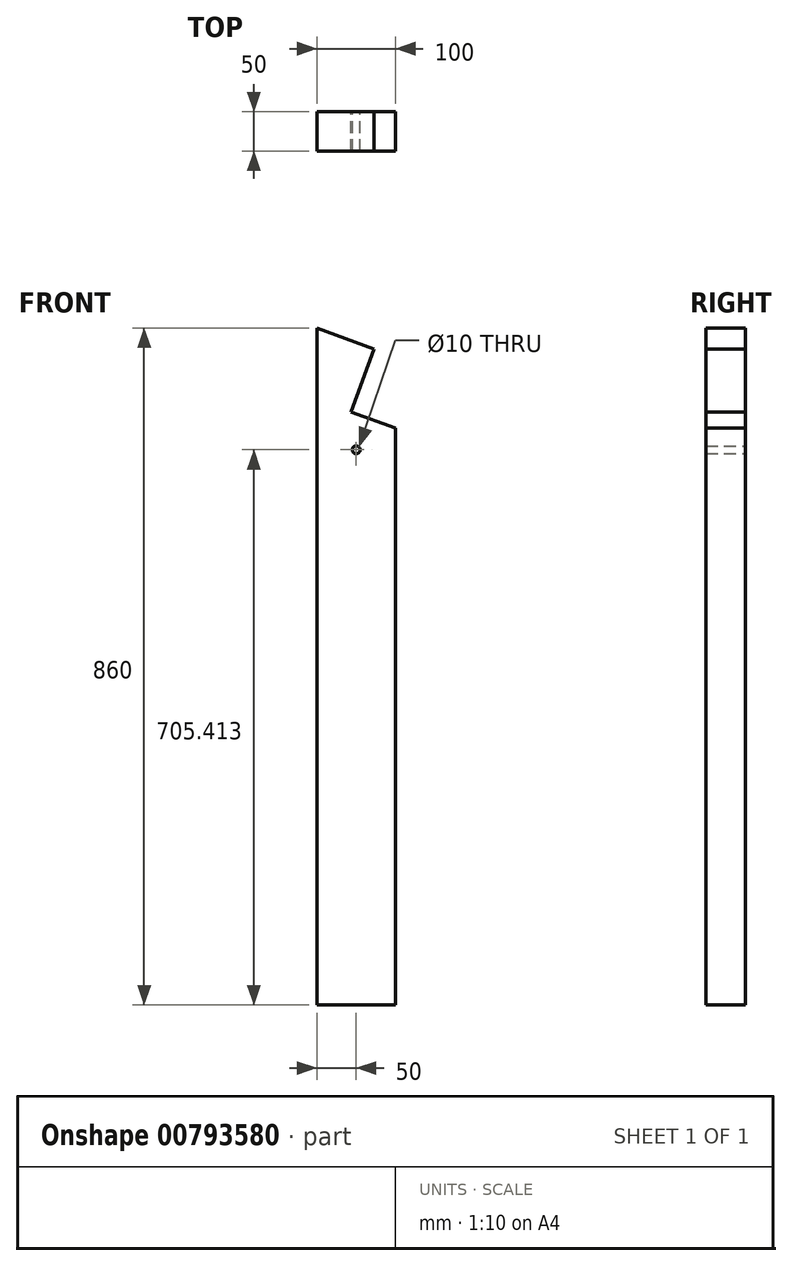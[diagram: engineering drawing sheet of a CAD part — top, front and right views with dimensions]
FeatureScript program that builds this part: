
annotation { "Feature Type Name" : "Feature", "Feature Type Description" : "" }
export const myFeature = defineFeature(function(context is Context, id is Id, definition is map)
    precondition{}
    {
        {
            var Q0;
            Q0=qCreatedBy(makeId("Front.planeOp"),FACE);
            var sketch = newSketch(context, id + "F0", { "sketchPlane" : qUnion([Q0])});
            skLineSegment(sketch, "E0.bottom", {"start": v(-100, 105.13) * mm, "end": v(0, 105.13) * mm});
            skLineSegment(sketch, "E0.top", {"start": v(-100, -754.87) * mm, "end": v(0, -754.87) * mm});
            skLineSegment(sketch, "E0.left", {"start": v(-100, 105.13) * mm, "end": v(-100, -754.87) * mm});
            skLineSegment(sketch, "E0.right", {"start": v(0, 105.13) * mm, "end": v(0, -754.87) * mm});
            skLineSegment(sketch, "E1", {"start": v(-100, 105.13) * mm, "end": v(0, 68.73) * mm});
            skLineSegment(sketch, "E2", {"start": v(-27.3, 78.67) * mm, "end": v(-56.38, -1.2) * mm});
            skLineSegment(sketch, "E3", {"start": v(-56.38, -1.2) * mm, "end": v(0, -21.73) * mm});
            skCircle(sketch, "E4", {"center": v(-50, -49.46) * mm, "radius": 5 * mm});
            skLineSegment(sketch, "E5", {"start": v(-50, 105.13) * mm, "end": v(-50, -143.54) * mm, "construction": true});
            skLineSegment(sketch, "E6", {"start": v(-35.24, -8.9) * mm, "end": v(-50, -49.46) * mm, "construction": true});
            skSolve(sketch);
        }
        {
            var Q0;
            {var subQ1=sQuery(id+"F0.wireOp",EDGE,"E0.top");Q0=makeQuery(id+"F0.imprint","IMPRINT",FACE,{"disambiguationData":[TD([[makeQuery(id+"F0.imprint","IMPRINT",EDGE,{"derivedFrom":subQ1}),1.0]])]});}
            extrude(context, id + "F1", {"entities" : qUnion([Q0]), "depth" : 50 * mm, "offsetDistance" : 25 * mm});
        }
    });
